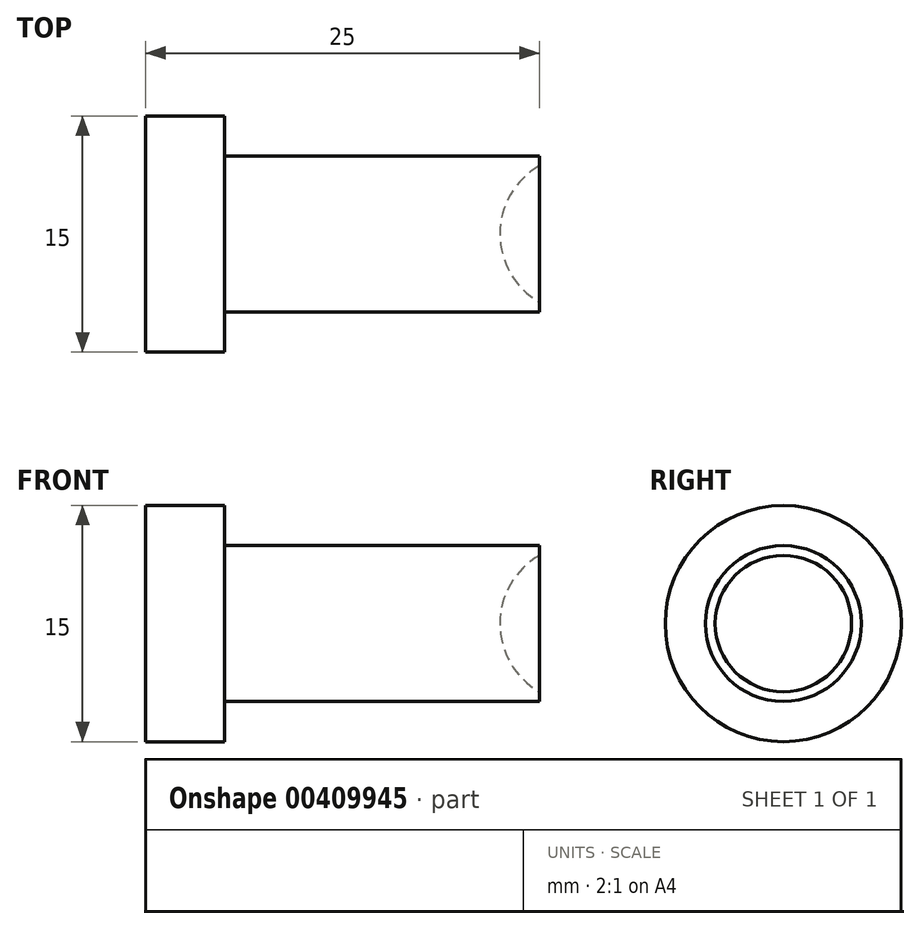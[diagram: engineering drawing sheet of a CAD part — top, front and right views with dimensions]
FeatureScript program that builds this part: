
annotation { "Feature Type Name" : "Feature", "Feature Type Description" : "" }
export const myFeature = defineFeature(function(context is Context, id is Id, definition is map)
    precondition{}
    {
        {
            var Q0;
            Q0=qCreatedBy(makeId("Front.planeOp"),FACE);
            var sketch = newSketch(context, id + "F0", { "sketchPlane" : qUnion([Q0])});
            skLineSegment(sketch, "E0.bottom", {"start": v(0, 0) * mm, "end": v(-5, 0) * mm});
            skLineSegment(sketch, "E0.top", {"start": v(0, 7.5) * mm, "end": v(-5, 7.5) * mm});
            skLineSegment(sketch, "E0.left", {"start": v(0, 4.95) * mm, "end": v(0, 7.5) * mm});
            skLineSegment(sketch, "E0.right", {"start": v(-5, 0) * mm, "end": v(-5, 7.5) * mm});
            skLineSegment(sketch, "E1.bottom", {"start": v(0, 0) * mm, "end": v(20, 0) * mm});
            skLineSegment(sketch, "E1.top", {"start": v(0, 4.95) * mm, "end": v(20, 4.95) * mm});
            skLineSegment(sketch, "E1.right", {"start": v(20, 0) * mm, "end": v(20, 4.95) * mm});
            skLineSegment(sketch, "E2", {"start": v(-13.4, 0) * mm, "end": v(22.5, 0) * mm, "construction": true});
            skPoint(sketch, "E2.endSnap0", {"position": v(10, 0) * mm});
            skSolve(sketch);
        }
        {
            var Q0;
            Q0=makeQuery(id+"F0.imprint","IMPRINT",FACE,{"disambiguationData":[TD([[makeQuery(id+"F0.imprint","IMPRINT",EDGE,{"derivedFrom":sQuery(id+"F0.wireOp",EDGE,"E0.bottom")}),-1.0]])]});
            var Q1;
            Q1=sQuery(id+"F0.wireOp",EDGE,"E2");
            revolve(context, id + "F1", {"entities" : qUnion([Q0]), "axis" : qUnion([Q1]), "revolveType" : RevolveType.FULL});
        }
        {
            var Q0;
            Q0=qCreatedBy(makeId("Front.planeOp"),FACE);
            var sketch = newSketch(context, id + "F2", { "sketchPlane" : qUnion([Q0])});
            skArc(sketch, "E3", {"start": v(22.5, -5) * mm, "mid": v(27.5, 0) * mm, "end": v(22.5, 5) * mm});
            skLineSegment(sketch, "E4", {"start": v(22.5, 0) * mm, "end": v(22.5, 10.04) * mm, "construction": true});
            skLineSegment(sketch, "E5", {"start": v(22.5, 10.04) * mm, "end": v(22.5, -10.81) * mm, "construction": true});
            skLineSegment(sketch, "E6", {"start": v(22.5, 5) * mm, "end": v(22.5, -5) * mm});
            skSolve(sketch);
        }
        {
            var Q0;
            Q0=makeQuery(id+"F2.imprint","IMPRINT",FACE,{"disambiguationData":[TD([[makeQuery(id+"F2.imprint","IMPRINT",EDGE,{"derivedFrom":sQuery(id+"F2.wireOp",EDGE,"E3")}),1.0]])]});
            var Q1;
            Q1=sQuery(id+"F2.wireOp",EDGE,"E5");
            revolve(context, id + "F3", {"operationType" : NewBodyOperationType.REMOVE, "entities" : qUnion([Q0]), "axis" : qUnion([Q1]), "revolveType" : RevolveType.FULL, "oppositeDirection" : true});
        }
    });
